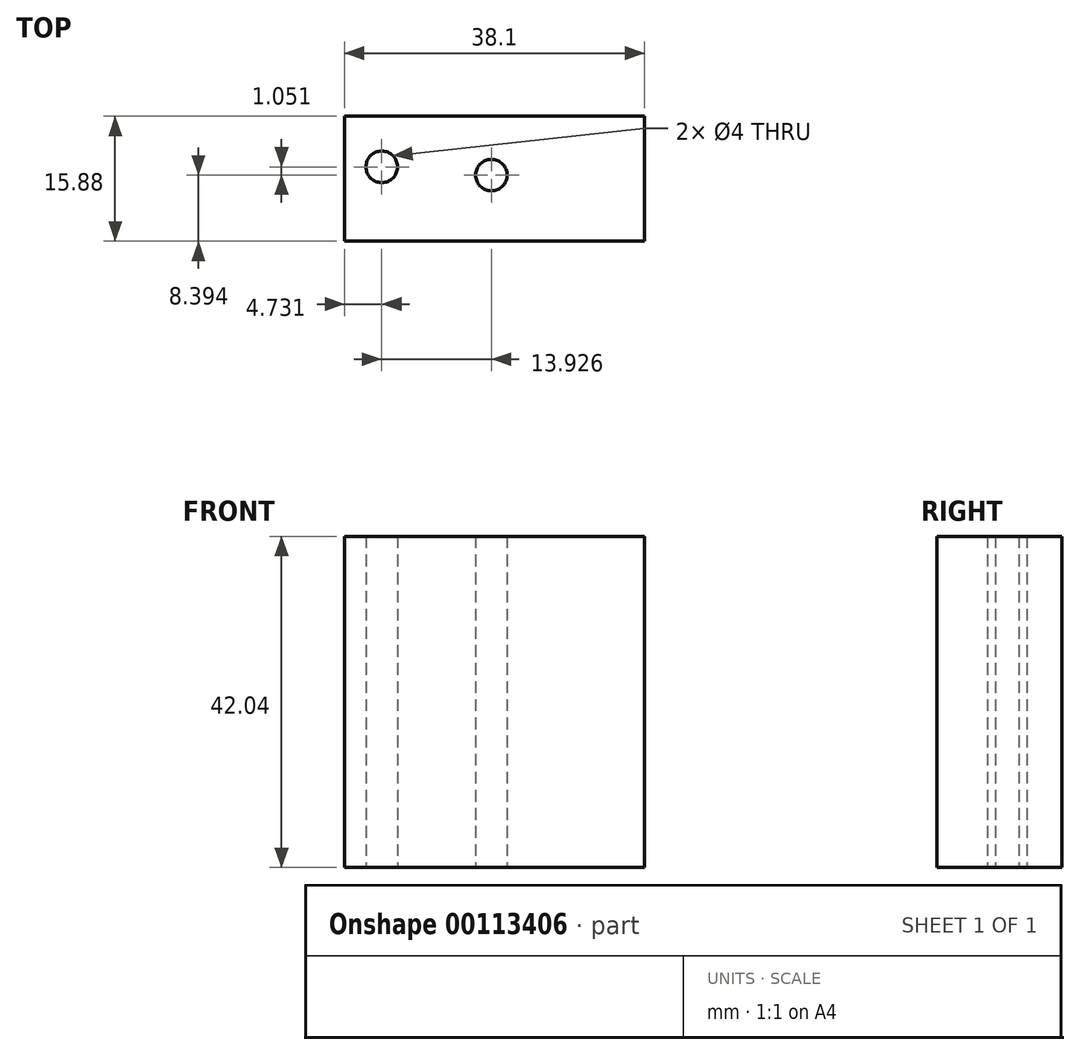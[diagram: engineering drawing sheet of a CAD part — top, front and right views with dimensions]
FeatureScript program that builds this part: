
annotation { "Feature Type Name" : "Feature", "Feature Type Description" : "" }
export const myFeature = defineFeature(function(context is Context, id is Id, definition is map)
    precondition{}
    {
        {
            var Q0;
            Q0=qCreatedBy(makeId("Front.planeOp"),FACE);
            var sketch = newSketch(context, id + "F0", { "sketchPlane" : qUnion([Q0])});
            skLineSegment(sketch, "E0.bottom", {"start": v(11.56, 0) * mm, "end": v(-26.54, 0) * mm});
            skLineSegment(sketch, "E0.top", {"start": v(11.56, 42.04) * mm, "end": v(-26.54, 42.04) * mm});
            skLineSegment(sketch, "E0.left", {"start": v(11.56, 0) * mm, "end": v(11.56, 42.04) * mm});
            skLineSegment(sketch, "E0.right", {"start": v(-26.54, 0) * mm, "end": v(-26.54, 42.04) * mm});
            skSolve(sketch);
        }
        {
            var Q0;
            Q0=makeQuery(id+"F0.imprint","IMPRINT",FACE,{"disambiguationData":[TD([[makeQuery(id+"F0.imprint","IMPRINT",EDGE,{"derivedFrom":sQuery(id+"F0.wireOp",EDGE,"E0.bottom")}),-1.0]])]});
            extrude(context, id + "F1", {"entities" : qUnion([Q0]), "depth" : 15.88 * mm});
        }
        {
            var Q0;
            Q0=makeQuery(id+"F1.opExtrude","SWEPT_FACE",FACE,{"disambiguationData":[OSD([sQuery(id+"F0.wireOp",EDGE,"E0.bottom")])]});
            var sketch = newSketch(context, id + "F2", { "sketchPlane" : qUnion([Q0])});
            skCircle(sketch, "E1", {"center": v(-21.8, 6.43) * mm, "radius": 3.94 * mm});
            skCircle(sketch, "E2", {"center": v(-7.88, 7.49) * mm, "radius": 4.24 * mm});
            skSolve(sketch);
        }
        {
            var Q0;
            Q0=sQuery(id+"F2.wireOp",VERTEX,"E2.center");
            var Q1;
            Q1=sQuery(id+"F2.wireOp",VERTEX,"E1.center");
            var Q2;
            Q2=makeQuery(id+"F1.opExtrude","SWEPT_BODY",BODY,{"disambiguationData":[OSD([sQuery(id+"F0.wireOp",EDGE,"E0.bottom"),sQuery(id+"F0.wireOp",EDGE,"E0.top"),sQuery(id+"F0.wireOp",EDGE,"E0.left"),sQuery(id+"F0.wireOp",EDGE,"E0.right")])]});
            hole(context, id + "F3", {"style" : HoleStyle.SIMPLE, "endStyle" : HoleEndStyle.THROUGH, "holeDiameter" : 4 * mm, "locations" : qUnion([Q0, Q1]), "scope" : qUnion([Q2]), "isTappedThrough" : true});
        }
    });
